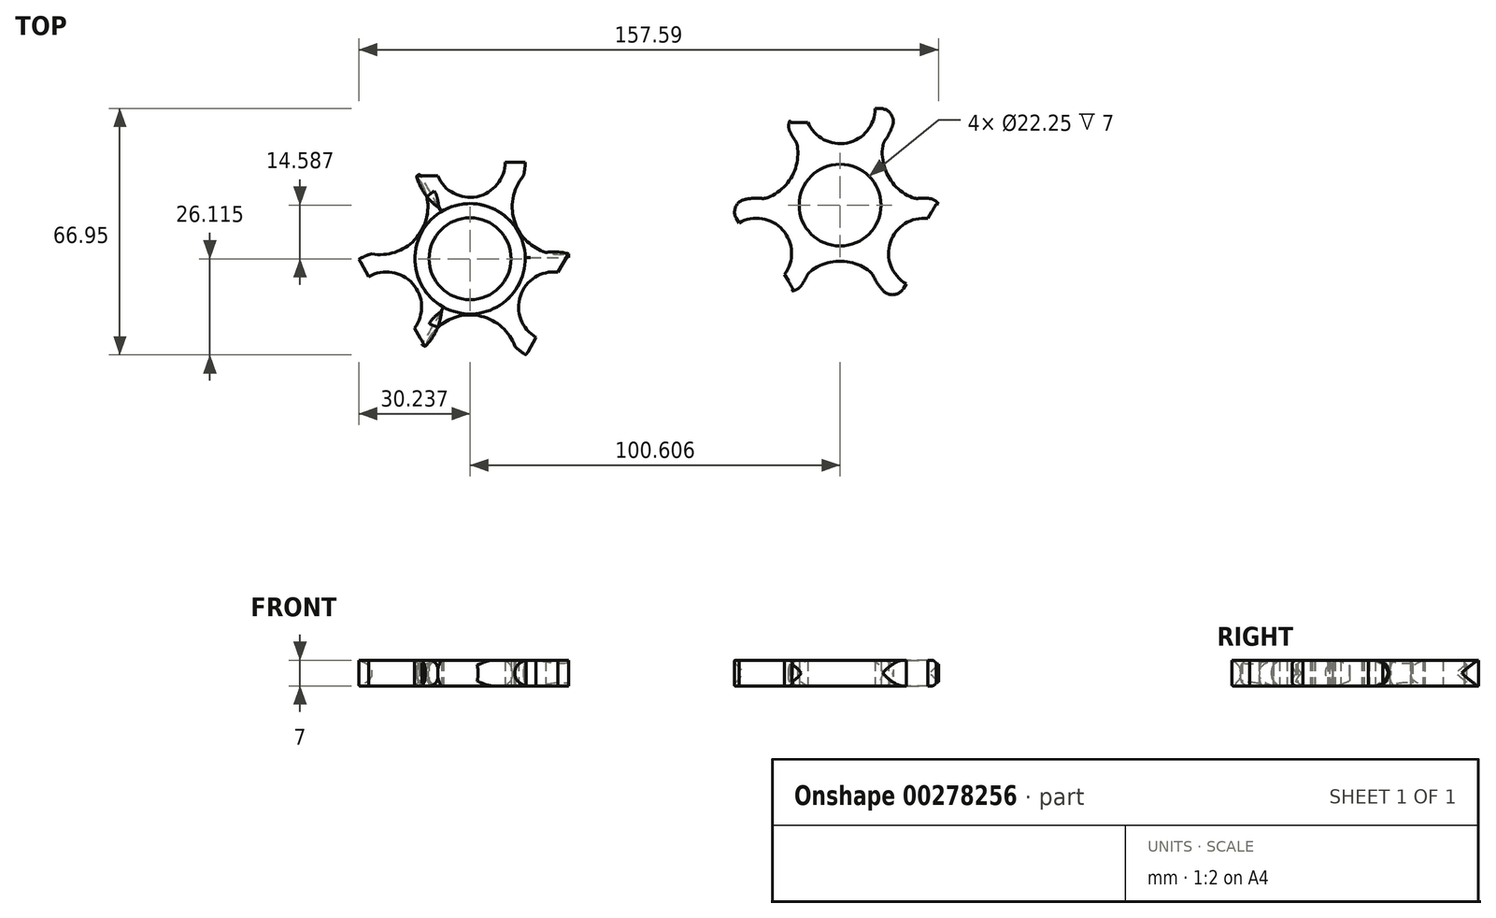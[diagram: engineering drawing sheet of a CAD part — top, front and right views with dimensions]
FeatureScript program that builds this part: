
annotation { "Feature Type Name" : "Feature", "Feature Type Description" : "" }
export const myFeature = defineFeature(function(context is Context, id is Id, definition is map)
    precondition{}
    {
        {
            var Q0;
            Q0=qCreatedBy(makeId("Top.planeOp"),FACE);
            var sketch = newSketch(context, id + "F0", { "sketchPlane" : qUnion([Q0])});
            skCircle(sketch, "E0", {"center": v(37.2, 27.44) * mm, "radius": 15 * mm});
            skLineSegment(sketch, "E1", {"start": v(37.2, 12.44) * mm, "end": v(37.2, 1.2) * mm});
            skCircle(sketch, "E2", {"center": v(37.2, 1.2) * mm, "radius": 15 * mm});
            skCircle(sketch, "E3", {"center": v(37.2, 1.2) * mm, "radius": 11.12 * mm});
            skLineSegment(sketch, "E4", {"start": v(37.2, 27.44) * mm, "end": v(22.2, 27.44) * mm});
            skLineSegment(sketch, "E5", {"start": v(22.2, 27.44) * mm, "end": v(37.2, 27.44) * mm});
            skLineSegment(sketch, "E6", {"start": v(37.2, 27.44) * mm, "end": v(52.2, 27.44) * mm});
            skLineSegment(sketch, "E7", {"start": v(37.2, 27.44) * mm, "end": v(25.65, 17.88) * mm, "construction": true});
            skLineSegment(sketch, "E8", {"start": v(25.65, 17.88) * mm, "end": v(31.43, 22.66) * mm, "construction": true});
            skLineSegment(sketch, "E9", {"start": v(37.2, 16.2) * mm, "end": v(37.2, 23.7) * mm});
            skLineSegment(sketch, "E10", {"start": v(37.2, 23.7) * mm, "end": v(22.68, 23.7) * mm});
            skLineSegment(sketch, "E11", {"start": v(37.2, 23.7) * mm, "end": v(51.73, 23.7) * mm});
            skArc(sketch, "E12", {"start": v(51.73, 23.7) * mm, "mid": v(50.41, 8.82) * mm, "end": v(63.95, 2.52) * mm});
            skPoint(sketch, "E13.0.midPoint", {"position": v(37.2, 21.1) * mm});
            skLineSegment(sketch, "E14", {"start": v(63.95, 2.52) * mm, "end": v(63.95, 1.52) * mm});
            skLineSegment(sketch, "E15", {"start": v(63.95, 1.52) * mm, "end": v(52.2, 1.52) * mm});
            skCircle(sketch, "E16", {"center": v(37.2, 27.44) * mm, "radius": 9.55 * mm});
            skArc(sketch, "E17", {"start": v(14.91, 28.25) * mm, "mid": v(13.6, 13.38) * mm, "end": v(27.14, 7.08) * mm});
            skLineSegment(sketch, "E18", {"start": v(63.95, 2.52) * mm, "end": v(37.2, 2.52) * mm});
            skLineSegment(sketch, "E19", {"start": v(10.46, 2.52) * mm, "end": v(37.2, 2.52) * mm});
            skLineSegment(sketch, "E20", {"start": v(37.2, 23.7) * mm, "end": v(37.2, 1.2) * mm});
            skArc(sketch, "E21", {"start": v(10.46, 2.52) * mm, "mid": v(24, 8.82) * mm, "end": v(22.68, 23.7) * mm});
            skSolve(sketch);
        }
        {
            var Q0;
            {var subQ0=sQuery(id+"F0.wireOp",EDGE,"E5");var subQ1=sQuery(id+"F0.wireOp",EDGE,"E0");var subQ2=makeQuery(id+"F0.imprint","INTERSECT",VERTEX,{"derivedFrom":[subQ1,subQ0]});Q0=makeQuery(id+"F0.imprint","IMPRINT",FACE,{"disambiguationData":[TD([[makeQuery(id+"F0.imprint","IMPRINT",EDGE,{"disambiguationData":[TD([[subQ2,1.0]])],"derivedFrom":subQ1}),1.0]])]});}
            var Q1;
            {var subQ0=sQuery(id+"F0.wireOp",EDGE,"E5");var subQ1=sQuery(id+"F0.wireOp",EDGE,"E0");var subQ2=makeQuery(id+"F0.imprint","INTERSECT",VERTEX,{"derivedFrom":[subQ1,subQ0]});Q1=makeQuery(id+"F0.imprint","IMPRINT",FACE,{"disambiguationData":[TD([[makeQuery(id+"F0.imprint","IMPRINT",EDGE,{"disambiguationData":[TD([[subQ2,-1.0]])],"derivedFrom":subQ1}),1.0]])]});}
            var Q2;
            {var subQ0=sQuery(id+"F0.wireOp",EDGE,"E12");var subQ2=sQuery(id+"F0.wireOp",EDGE,"E0");var subQ11=makeQuery(id+"F0.imprint","INTERSECT",VERTEX,{"derivedFrom":[subQ2,subQ0]});Q2=makeQuery(id+"F0.imprint","IMPRINT",FACE,{"disambiguationData":[TD([[makeQuery(id+"F0.imprint","IMPRINT",EDGE,{"disambiguationData":[TD([[subQ11,1.0]])],"derivedFrom":subQ2}),1.0]])]});}
            var Q3;
            {var subQ4=sQuery(id+"F0.wireOp",EDGE,"E3");Q3=makeQuery(id+"F0.imprint","IMPRINT",FACE,{"disambiguationData":[TD([[makeQuery(id+"F0.imprint","IMPRINT",EDGE,{"derivedFrom":subQ4}),-1.0]])]});}
            var Q4;
            {var subQ0=sQuery(id+"F0.wireOp",EDGE,"E0");var subQ1=makeQuery(id+"F0.imprint","INTERSECT",VERTEX,{"derivedFrom":[subQ0,sQuery(id+"F0.wireOp",EDGE,"E3")]});Q4=makeQuery(id+"F0.imprint","IMPRINT",FACE,{"disambiguationData":[TD([[makeQuery(id+"F0.imprint","IMPRINT",EDGE,{"disambiguationData":[TD([[subQ1,1.0]])],"derivedFrom":subQ0}),1.0]])]});}
            var Q5;
            {var subQ0=sQuery(id+"F0.wireOp",EDGE,"E6");var subQ1=sQuery(id+"F0.wireOp",EDGE,"E0");var subQ2=makeQuery(id+"F0.imprint","INTERSECT",VERTEX,{"derivedFrom":[subQ1,subQ0]});Q5=makeQuery(id+"F0.imprint","IMPRINT",FACE,{"disambiguationData":[TD([[makeQuery(id+"F0.imprint","IMPRINT",EDGE,{"disambiguationData":[TD([[subQ2,1.0]])],"derivedFrom":subQ0}),-1.0]])]});}
            var Q6;
            {var subQ0=sQuery(id+"F0.wireOp",EDGE,"E14");Q6=makeQuery(id+"F0.imprint","IMPRINT",FACE,{"disambiguationData":[TD([[makeQuery(id+"F0.imprint","IMPRINT",EDGE,{"derivedFrom":subQ0}),-1.0]])]});}
            var Q7;
            {var subQ0=sQuery(id+"F0.wireOp",EDGE,"E2");var subQ1=sQuery(id+"F0.wireOp",EDGE,"E0");var subQ2=makeQuery(id+"F0.imprint","INTERSECT",VERTEX,{"disambiguationData":[OD(1.0)],"derivedFrom":[subQ1,subQ0]});Q7=makeQuery(id+"F0.imprint","IMPRINT",FACE,{"disambiguationData":[TD([[makeQuery(id+"F0.imprint","IMPRINT",EDGE,{"disambiguationData":[TD([[subQ2,-1.0]])],"derivedFrom":subQ0}),1.0]])]});}
            var Q8;
            {var subQ0=sQuery(id+"F0.wireOp",EDGE,"E12");var subQ1=sQuery(id+"F0.wireOp",EDGE,"E0");var subQ2=makeQuery(id+"F0.imprint","INTERSECT",VERTEX,{"derivedFrom":[subQ1,subQ0]});Q8=makeQuery(id+"F0.imprint","IMPRINT",FACE,{"disambiguationData":[TD([[makeQuery(id+"F0.imprint","IMPRINT",EDGE,{"disambiguationData":[TD([[subQ2,1.0]])],"derivedFrom":subQ1}),-1.0]])]});}
            var Q9;
            {var subQ5=sQuery(id+"F0.wireOp",EDGE,"E2");var subQ6=makeQuery(id+"F0.imprint","INTERSECT",VERTEX,{"derivedFrom":[subQ5,sQuery(id+"F0.wireOp",EDGE,"E17")]});Q9=makeQuery(id+"F0.imprint","IMPRINT",FACE,{"disambiguationData":[TD([[makeQuery(id+"F0.imprint","IMPRINT",EDGE,{"disambiguationData":[TD([[subQ6,1.0]])],"derivedFrom":subQ5}),1.0]])]});}
            var Q10;
            {var subQ6=sQuery(id+"F0.wireOp",EDGE,"E0");var subQ9=sQuery(id+"F0.wireOp",EDGE,"E21");var subQ11=makeQuery(id+"F0.imprint","INTERSECT",VERTEX,{"derivedFrom":[subQ6,subQ9]});Q10=makeQuery(id+"F0.imprint","IMPRINT",FACE,{"disambiguationData":[TD([[makeQuery(id+"F0.imprint","IMPRINT",EDGE,{"disambiguationData":[TD([[subQ11,-1.0]])],"derivedFrom":subQ6}),1.0]])]});}
            var Q11;
            {var subQ0=sQuery(id+"F0.wireOp",EDGE,"E21");var subQ1=sQuery(id+"F0.wireOp",EDGE,"E0");var subQ2=makeQuery(id+"F0.imprint","INTERSECT",VERTEX,{"derivedFrom":[subQ1,subQ0]});Q11=makeQuery(id+"F0.imprint","IMPRINT",FACE,{"disambiguationData":[TD([[makeQuery(id+"F0.imprint","IMPRINT",EDGE,{"disambiguationData":[TD([[subQ2,-1.0]])],"derivedFrom":subQ1}),-1.0]])]});}
            var Q12;
            {var subQ5=sQuery(id+"F0.wireOp",EDGE,"E2");var subQ7=makeQuery(id+"F0.imprint","INTERSECT",VERTEX,{"derivedFrom":[subQ5,sQuery(id+"F0.wireOp",EDGE,"E15")]});Q12=makeQuery(id+"F0.imprint","IMPRINT",FACE,{"disambiguationData":[TD([[makeQuery(id+"F0.imprint","IMPRINT",EDGE,{"disambiguationData":[TD([[subQ7,-1.0]])],"derivedFrom":subQ5}),1.0]])]});}
            extrude(context, id + "F1", {"entities" : qUnion([Q0, Q1, Q2, Q3, Q4, Q5, Q6, Q7, Q8, Q9, Q10, Q11, Q12]), "depth" : 7 * mm, "offsetDistance" : 25 * mm});
        }
        {
            var Q0;
            Q0=makeQuery(id+"F0.imprint","IMPRINT",FACE,{"disambiguationData":[TD([[makeQuery(id+"F0.imprint","IMPRINT",EDGE,{"derivedFrom":sQuery(id+"F0.wireOp",EDGE,"E3")}),1.0]])]});
            var Q1;
            Q1=sQuery(id+"F0.wireOp",EDGE,"E1");
            extrude(context, id + "F2", {"entities" : qUnion([Q0]), "bodyType" : ExtendedToolBodyType.SURFACE, "surfaceEntities" : qUnion([Q1]), "depth" : 25 * mm, "offsetDistance" : 25 * mm});
        }
        {
            var Q0;
            Q0=makeQuery(id+"F1.opExtrude","SWEPT_BODY",BODY,{"disambiguationData":[OSD([sQuery(id+"F0.wireOp",EDGE,"E0"),sQuery(id+"F0.wireOp",EDGE,"E2"),sQuery(id+"F0.wireOp",EDGE,"E3"),sQuery(id+"F0.wireOp",EDGE,"E12"),sQuery(id+"F0.wireOp",EDGE,"E14"),sQuery(id+"F0.wireOp",EDGE,"E15"),sQuery(id+"F0.wireOp",EDGE,"E16")])]});
            var Q1;
            Q1=makeQuery(id+"F2.opExtrude","SWEPT_EDGE",EDGE,{"disambiguationData":[OSD([sQuery(id+"F0.wireOp",VERTEX,"E1.end")])]});
            circularPattern(context, id + "F3", {"entities" : qUnion([Q0]), "axis" : qUnion([Q1]), "angle" : 360 * degree, "instanceCount" : 3, "equalSpace" : true, "computeTransformsWithoutBuiltin" : true});
        }
        {
            var Q0;
            Q0=makeQuery(id+"F3.opPattern","COPY",BODY,{"derivedFrom":makeQuery(id+"F1.opExtrude","SWEPT_BODY",BODY,{"disambiguationData":[OSD([sQuery(id+"F0.wireOp",EDGE,"E0"),sQuery(id+"F0.wireOp",EDGE,"E2"),sQuery(id+"F0.wireOp",EDGE,"E3"),sQuery(id+"F0.wireOp",EDGE,"E12"),sQuery(id+"F0.wireOp",EDGE,"E14"),sQuery(id+"F0.wireOp",EDGE,"E15"),sQuery(id+"F0.wireOp",EDGE,"E16"),sQuery(id+"F0.wireOp",EDGE,"E17"),sQuery(id+"F0.wireOp",EDGE,"E21")])]}),"instanceName":"2"});
            var Q1;
            Q1=makeQuery(id+"F1.opExtrude","SWEPT_BODY",BODY,{"disambiguationData":[OSD([sQuery(id+"F0.wireOp",EDGE,"E0"),sQuery(id+"F0.wireOp",EDGE,"E2"),sQuery(id+"F0.wireOp",EDGE,"E3"),sQuery(id+"F0.wireOp",EDGE,"E12"),sQuery(id+"F0.wireOp",EDGE,"E14"),sQuery(id+"F0.wireOp",EDGE,"E15"),sQuery(id+"F0.wireOp",EDGE,"E16"),sQuery(id+"F0.wireOp",EDGE,"E17"),sQuery(id+"F0.wireOp",EDGE,"E21")])]});
            var Q2;
            Q2=makeQuery(id+"F3.opPattern","COPY",BODY,{"derivedFrom":makeQuery(id+"F1.opExtrude","SWEPT_BODY",BODY,{"disambiguationData":[OSD([sQuery(id+"F0.wireOp",EDGE,"E0"),sQuery(id+"F0.wireOp",EDGE,"E2"),sQuery(id+"F0.wireOp",EDGE,"E3"),sQuery(id+"F0.wireOp",EDGE,"E12"),sQuery(id+"F0.wireOp",EDGE,"E14"),sQuery(id+"F0.wireOp",EDGE,"E15"),sQuery(id+"F0.wireOp",EDGE,"E16"),sQuery(id+"F0.wireOp",EDGE,"E17"),sQuery(id+"F0.wireOp",EDGE,"E21")])]}),"instanceName":"1"});
            booleanBodies(context, id + "F4", {"operationType" : BooleanOperationType.UNION, "tools" : qUnion([Q0, Q1, Q2])});
        }
        {
            var Q0;
            Q0=makeQuery(id+"F4.opBoolean","MERGE",FACE,{"derivedFrom":[makeQuery(id+"F1.opExtrude","SWEPT_FACE",FACE,{"disambiguationData":[OSD([sQuery(id+"F0.wireOp",EDGE,"E21")])]}),makeQuery(id+"F3.opPattern","COPY",FACE,{"derivedFrom":makeQuery(id+"F1.opExtrude","SWEPT_FACE",FACE,{"disambiguationData":[OSD([sQuery(id+"F0.wireOp",EDGE,"E12")])]}),"instanceName":"1"})]});
            var Q1;
            Q1=makeQuery(id+"F3.opPattern","COPY",FACE,{"derivedFrom":makeQuery(id+"F1.opExtrude","SWEPT_FACE",FACE,{"disambiguationData":[OSD([sQuery(id+"F0.wireOp",EDGE,"E0")])]}),"instanceName":"1"});
            var Q2;
            Q2=makeQuery(id+"F1.opExtrude","SWEPT_FACE",FACE,{"disambiguationData":[OSD([sQuery(id+"F0.wireOp",EDGE,"E0")])]});
            var Q3;
            Q3=makeQuery(id+"F4.opBoolean","MERGE",FACE,{"derivedFrom":[makeQuery(id+"F1.opExtrude","SWEPT_FACE",FACE,{"disambiguationData":[OSD([sQuery(id+"F0.wireOp",EDGE,"E12")])]}),makeQuery(id+"F3.opPattern","COPY",FACE,{"derivedFrom":makeQuery(id+"F1.opExtrude","SWEPT_FACE",FACE,{"disambiguationData":[OSD([sQuery(id+"F0.wireOp",EDGE,"E21")])]}),"instanceName":"2"})]});
            var Q4;
            Q4=makeQuery(id+"F3.opPattern","COPY",FACE,{"derivedFrom":makeQuery(id+"F1.opExtrude","SWEPT_FACE",FACE,{"disambiguationData":[OSD([sQuery(id+"F0.wireOp",EDGE,"E12")])]}),"instanceName":"2"});
            var Q5;
            Q5=makeQuery(id+"F3.opPattern","COPY",FACE,{"derivedFrom":makeQuery(id+"F1.opExtrude","SWEPT_FACE",FACE,{"disambiguationData":[OSD([sQuery(id+"F0.wireOp",EDGE,"E0")])]}),"instanceName":"2"});
            fillet(context, id + "F5", {"entities" : qUnion([Q0, Q1, Q2, Q3, Q4, Q5]), "radius" : 3.5 * mm, "tangentPropagation" : true, "allowEdgeOverflow" : false});
        }
        {
            var Q0;
            Q0=qCreatedBy(makeId("Top.planeOp"),FACE);
            var sketch = newSketch(context, id + "F6", { "sketchPlane" : qUnion([Q0])});
            skCircle(sketch, "E22", {"center": v(-63.4, 12.86) * mm, "radius": 15 * mm});
            skLineSegment(sketch, "E23", {"start": v(-63.4, -2.14) * mm, "end": v(-63.4, -13.4) * mm});
            skCircle(sketch, "E24", {"center": v(-63.4, -13.4) * mm, "radius": 15 * mm});
            skCircle(sketch, "E25", {"center": v(-63.4, -13.4) * mm, "radius": 11.12 * mm});
            skLineSegment(sketch, "E26", {"start": v(-63.4, 12.86) * mm, "end": v(-78.4, 12.86) * mm});
            skLineSegment(sketch, "E27", {"start": v(-78.4, 12.86) * mm, "end": v(-63.4, 12.86) * mm});
            skLineSegment(sketch, "E28", {"start": v(-63.4, 12.86) * mm, "end": v(-48.4, 12.86) * mm});
            skLineSegment(sketch, "E29", {"start": v(-63.4, 12.86) * mm, "end": v(-74.96, 3.29) * mm, "construction": true});
            skLineSegment(sketch, "E30", {"start": v(-74.96, 3.29) * mm, "end": v(-69.18, 8.07) * mm, "construction": true});
            skLineSegment(sketch, "E31", {"start": v(-63.4, 1.6) * mm, "end": v(-63.4, 9.1) * mm});
            skLineSegment(sketch, "E32", {"start": v(-63.4, 9.1) * mm, "end": v(-77.93, 9.1) * mm});
            skLineSegment(sketch, "E33", {"start": v(-63.4, 9.1) * mm, "end": v(-48.88, 9.1) * mm});
            skArc(sketch, "E34", {"start": v(-48.88, 9.1) * mm, "mid": v(-50.2, -5.77) * mm, "end": v(-36.66, -12.07) * mm});
            skPoint(sketch, "E35.0.midPoint", {"position": v(-63.4, 6.5) * mm});
            skLineSegment(sketch, "E36", {"start": v(-36.66, -12.07) * mm, "end": v(-36.66, -13.07) * mm});
            skLineSegment(sketch, "E37", {"start": v(-36.66, -13.07) * mm, "end": v(-48.4, -13.07) * mm});
            skCircle(sketch, "E38", {"center": v(-63.4, 12.86) * mm, "radius": 9.55 * mm});
            skArc(sketch, "E39", {"start": v(-85.7, 13.66) * mm, "mid": v(-87, -1.21) * mm, "end": v(-73.47, -7.51) * mm});
            skLineSegment(sketch, "E40", {"start": v(-36.66, -12.07) * mm, "end": v(-63.4, -12.07) * mm});
            skLineSegment(sketch, "E41", {"start": v(-90.15, -12.07) * mm, "end": v(-63.4, -12.07) * mm});
            skLineSegment(sketch, "E42", {"start": v(-63.4, 9.1) * mm, "end": v(-63.4, -13.4) * mm});
            skArc(sketch, "E43", {"start": v(-90.15, -12.07) * mm, "mid": v(-76.61, -5.77) * mm, "end": v(-77.93, 9.1) * mm});
            skLineSegment(sketch, "E44", {"start": v(-63.4, -13.4) * mm, "end": v(-65.58, -14.12) * mm});
            skSolve(sketch);
        }
        {
            var Q0;
            {var subQ0=sQuery(id+"F6.wireOp",EDGE,"E27");var subQ1=sQuery(id+"F6.wireOp",EDGE,"E22");var subQ2=makeQuery(id+"F6.imprint","INTERSECT",VERTEX,{"derivedFrom":[subQ1,subQ0]});Q0=makeQuery(id+"F6.imprint","IMPRINT",FACE,{"disambiguationData":[TD([[makeQuery(id+"F6.imprint","IMPRINT",EDGE,{"disambiguationData":[TD([[subQ2,1.0]])],"derivedFrom":subQ1}),1.0]])]});}
            var Q1;
            {var subQ0=sQuery(id+"F6.wireOp",EDGE,"E27");var subQ1=sQuery(id+"F6.wireOp",EDGE,"E22");var subQ2=makeQuery(id+"F6.imprint","INTERSECT",VERTEX,{"derivedFrom":[subQ1,subQ0]});Q1=makeQuery(id+"F6.imprint","IMPRINT",FACE,{"disambiguationData":[TD([[makeQuery(id+"F6.imprint","IMPRINT",EDGE,{"disambiguationData":[TD([[subQ2,-1.0]])],"derivedFrom":subQ0}),-1.0]])]});}
            var Q2;
            {var subQ6=sQuery(id+"F6.wireOp",EDGE,"E22");var subQ9=sQuery(id+"F6.wireOp",EDGE,"E43");var subQ11=makeQuery(id+"F6.imprint","INTERSECT",VERTEX,{"derivedFrom":[subQ6,subQ9]});Q2=makeQuery(id+"F6.imprint","IMPRINT",FACE,{"disambiguationData":[TD([[makeQuery(id+"F6.imprint","IMPRINT",EDGE,{"disambiguationData":[TD([[subQ11,-1.0]])],"derivedFrom":subQ6}),1.0]])]});}
            var Q3;
            {var subQ0=sQuery(id+"F6.wireOp",EDGE,"E28");var subQ1=sQuery(id+"F6.wireOp",EDGE,"E22");var subQ2=makeQuery(id+"F6.imprint","INTERSECT",VERTEX,{"derivedFrom":[subQ1,subQ0]});Q3=makeQuery(id+"F6.imprint","IMPRINT",FACE,{"disambiguationData":[TD([[makeQuery(id+"F6.imprint","IMPRINT",EDGE,{"disambiguationData":[TD([[subQ2,1.0]])],"derivedFrom":subQ0}),-1.0]])]});}
            var Q4;
            {var subQ0=sQuery(id+"F6.wireOp",EDGE,"E34");var subQ2=sQuery(id+"F6.wireOp",EDGE,"E22");var subQ4=makeQuery(id+"F6.imprint","INTERSECT",VERTEX,{"derivedFrom":[subQ2,subQ0]});Q4=makeQuery(id+"F6.imprint","IMPRINT",FACE,{"disambiguationData":[TD([[makeQuery(id+"F6.imprint","IMPRINT",EDGE,{"disambiguationData":[TD([[subQ4,1.0]])],"derivedFrom":subQ2}),1.0]])]});}
            var Q5;
            {var subQ0=sQuery(id+"F6.wireOp",EDGE,"E42");var subQ1=sQuery(id+"F6.wireOp",EDGE,"E22");var subQ2=makeQuery(id+"F6.imprint","INTERSECT",VERTEX,{"derivedFrom":[subQ1,subQ0]});Q5=makeQuery(id+"F6.imprint","IMPRINT",FACE,{"disambiguationData":[TD([[makeQuery(id+"F6.imprint","IMPRINT",EDGE,{"disambiguationData":[TD([[subQ2,-1.0]])],"derivedFrom":subQ1}),1.0]])]});}
            var Q6;
            {var subQ0=sQuery(id+"F6.wireOp",EDGE,"E24");var subQ1=sQuery(id+"F6.wireOp",EDGE,"E22");var subQ2=makeQuery(id+"F6.imprint","INTERSECT",VERTEX,{"disambiguationData":[OD(0.0)],"derivedFrom":[subQ1,subQ0]});Q6=makeQuery(id+"F6.imprint","IMPRINT",FACE,{"disambiguationData":[TD([[makeQuery(id+"F6.imprint","IMPRINT",EDGE,{"disambiguationData":[TD([[subQ2,-1.0]])],"derivedFrom":subQ1}),1.0]])]});}
            var Q7;
            {var subQ5=sQuery(id+"F6.wireOp",EDGE,"E24");var subQ7=sQuery(id+"F6.wireOp",EDGE,"E22");var subQ8=makeQuery(id+"F6.imprint","INTERSECT",VERTEX,{"disambiguationData":[OD(0.0)],"derivedFrom":[subQ7,subQ5]});Q7=makeQuery(id+"F6.imprint","IMPRINT",FACE,{"disambiguationData":[TD([[makeQuery(id+"F6.imprint","IMPRINT",EDGE,{"disambiguationData":[TD([[subQ8,-1.0]])],"derivedFrom":subQ7}),-1.0]])]});}
            var Q8;
            {var subQ0=sQuery(id+"F6.wireOp",EDGE,"E42");var subQ5=sQuery(id+"F6.wireOp",EDGE,"E22");var subQ6=makeQuery(id+"F6.imprint","INTERSECT",VERTEX,{"derivedFrom":[subQ5,subQ0]});Q8=makeQuery(id+"F6.imprint","IMPRINT",FACE,{"disambiguationData":[TD([[makeQuery(id+"F6.imprint","IMPRINT",EDGE,{"disambiguationData":[TD([[subQ6,-1.0]])],"derivedFrom":subQ5}),-1.0]])]});}
            var Q9;
            {var subQ0=sQuery(id+"F6.wireOp",EDGE,"E34");var subQ1=sQuery(id+"F6.wireOp",EDGE,"E22");var subQ2=makeQuery(id+"F6.imprint","INTERSECT",VERTEX,{"derivedFrom":[subQ1,subQ0]});Q9=makeQuery(id+"F6.imprint","IMPRINT",FACE,{"disambiguationData":[TD([[makeQuery(id+"F6.imprint","IMPRINT",EDGE,{"disambiguationData":[TD([[subQ2,1.0]])],"derivedFrom":subQ1}),-1.0]])]});}
            var Q10;
            {var subQ0=sQuery(id+"F6.wireOp",EDGE,"E43");var subQ1=sQuery(id+"F6.wireOp",EDGE,"E22");var subQ2=makeQuery(id+"F6.imprint","INTERSECT",VERTEX,{"derivedFrom":[subQ1,subQ0]});Q10=makeQuery(id+"F6.imprint","IMPRINT",FACE,{"disambiguationData":[TD([[makeQuery(id+"F6.imprint","IMPRINT",EDGE,{"disambiguationData":[TD([[subQ2,-1.0]])],"derivedFrom":subQ1}),-1.0]])]});}
            var Q11;
            {var subQ5=sQuery(id+"F6.wireOp",EDGE,"E24");var subQ7=makeQuery(id+"F6.imprint","INTERSECT",VERTEX,{"derivedFrom":[subQ5,sQuery(id+"F6.wireOp",EDGE,"E37")]});Q11=makeQuery(id+"F6.imprint","IMPRINT",FACE,{"disambiguationData":[TD([[makeQuery(id+"F6.imprint","IMPRINT",EDGE,{"disambiguationData":[TD([[subQ7,-1.0]])],"derivedFrom":subQ5}),1.0]])]});}
            var Q12;
            {var subQ4=sQuery(id+"F6.wireOp",EDGE,"E36");Q12=makeQuery(id+"F6.imprint","IMPRINT",FACE,{"disambiguationData":[TD([[makeQuery(id+"F6.imprint","IMPRINT",EDGE,{"derivedFrom":subQ4}),-1.0]])]});}
            extrude(context, id + "F7", {"entities" : qUnion([Q0, Q1, Q2, Q3, Q4, Q5, Q6, Q7, Q8, Q9, Q10, Q11, Q12]), "depth" : 7 * mm, "offsetDistance" : 25 * mm});
        }
        {
            var Q0;
            Q0=sQuery(id+"F6.wireOp",EDGE,"E44");
            extrude(context, id + "F8", {"bodyType" : ExtendedToolBodyType.SURFACE, "surfaceEntities" : qUnion([Q0]), "depth" : 25 * mm, "offsetDistance" : 25 * mm});
        }
        {
            var Q0;
            Q0=makeQuery(id+"F7.opExtrude","SWEPT_BODY",BODY,{"disambiguationData":[OSD([sQuery(id+"F6.wireOp",EDGE,"E22"),sQuery(id+"F6.wireOp",EDGE,"E24"),sQuery(id+"F6.wireOp",EDGE,"E25"),sQuery(id+"F6.wireOp",EDGE,"E34"),sQuery(id+"F6.wireOp",EDGE,"E36"),sQuery(id+"F6.wireOp",EDGE,"E37"),sQuery(id+"F6.wireOp",EDGE,"E38"),sQuery(id+"F6.wireOp",EDGE,"E39"),sQuery(id+"F6.wireOp",EDGE,"E43")])]});
            var Q1;
            Q1=makeQuery(id+"F8.opExtrude","SWEPT_EDGE",EDGE,{"disambiguationData":[OSD([sQuery(id+"F6.wireOp",VERTEX,"E44.start")])]});
            circularPattern(context, id + "F9", {"operationType" : NewBodyOperationType.ADD, "entities" : qUnion([Q0]), "axis" : qUnion([Q1]), "angle" : 360 * degree, "instanceCount" : 3, "equalSpace" : true, "computeTransformsWithoutBuiltin" : true});
        }
        {
            var Q0;
            Q0=makeQuery(id+"F9.boolean.opBoolean","MERGE",EDGE,{"derivedFrom":[makeQuery(id+"F9.opPattern","COPY",EDGE,{"derivedFrom":makeQuery(id+"F7.opExtrude","CAP_EDGE",EDGE,{"disambiguationData":[OSD([sQuery(id+"F6.wireOp",EDGE,"E43")])],"isStart":false}),"instanceName":"1"}),makeQuery(id+"F9.opPattern","COPY",EDGE,{"derivedFrom":makeQuery(id+"F7.opExtrude","CAP_EDGE",EDGE,{"disambiguationData":[OSD([sQuery(id+"F6.wireOp",EDGE,"E34")])],"isStart":false}),"instanceName":"2"})]});
            var Q1;
            Q1=makeQuery(id+"F9.boolean.opBoolean","MERGE",EDGE,{"derivedFrom":[makeQuery(id+"F9.opPattern","COPY",EDGE,{"derivedFrom":makeQuery(id+"F7.opExtrude","CAP_EDGE",EDGE,{"disambiguationData":[OSD([sQuery(id+"F6.wireOp",EDGE,"E43")])],"isStart":true}),"instanceName":"1"}),makeQuery(id+"F9.opPattern","COPY",EDGE,{"derivedFrom":makeQuery(id+"F7.opExtrude","CAP_EDGE",EDGE,{"disambiguationData":[OSD([sQuery(id+"F6.wireOp",EDGE,"E34")])],"isStart":true}),"instanceName":"2"})]});
            var Q2;
            Q2=makeQuery(id+"F7.opExtrude","CAP_EDGE",EDGE,{"disambiguationData":[OSD([sQuery(id+"F6.wireOp",EDGE,"E34")])],"isStart":false});
            var Q3;
            Q3=makeQuery(id+"F7.opExtrude","CAP_EDGE",EDGE,{"disambiguationData":[OSD([sQuery(id+"F6.wireOp",EDGE,"E34")])],"isStart":true});
            var Q4;
            Q4=makeQuery(id+"F9.boolean.opBoolean","MERGE",EDGE,{"derivedFrom":[makeQuery(id+"F7.opExtrude","CAP_EDGE",EDGE,{"disambiguationData":[OSD([sQuery(id+"F6.wireOp",EDGE,"E43")])],"isStart":false}),makeQuery(id+"F9.opPattern","COPY",EDGE,{"derivedFrom":makeQuery(id+"F7.opExtrude","CAP_EDGE",EDGE,{"disambiguationData":[OSD([sQuery(id+"F6.wireOp",EDGE,"E34")])],"isStart":false}),"instanceName":"1"})]});
            var Q5;
            Q5=makeQuery(id+"F9.boolean.opBoolean","MERGE",EDGE,{"derivedFrom":[makeQuery(id+"F7.opExtrude","CAP_EDGE",EDGE,{"disambiguationData":[OSD([sQuery(id+"F6.wireOp",EDGE,"E43")])],"isStart":true}),makeQuery(id+"F9.opPattern","COPY",EDGE,{"derivedFrom":makeQuery(id+"F7.opExtrude","CAP_EDGE",EDGE,{"disambiguationData":[OSD([sQuery(id+"F6.wireOp",EDGE,"E34")])],"isStart":true}),"instanceName":"1"})]});
            fillet(context, id + "F10", {"entities" : qUnion([Q0, Q1, Q2, Q3, Q4, Q5]), "radius" : 3 * mm, "tangentPropagation" : true, "allowEdgeOverflow" : false});
        }
        {
            var Q0;
            Q0=makeQuery(id+"F9.opPattern","COPY",EDGE,{"derivedFrom":makeQuery(id+"F7.opExtrude","CAP_EDGE",EDGE,{"disambiguationData":[OSD([sQuery(id+"F6.wireOp",EDGE,"E22")])],"isStart":false}),"instanceName":"2"});
            var Q1;
            Q1=makeQuery(id+"F9.opPattern","COPY",EDGE,{"derivedFrom":makeQuery(id+"F7.opExtrude","CAP_EDGE",EDGE,{"disambiguationData":[OSD([sQuery(id+"F6.wireOp",EDGE,"E22")])],"isStart":true}),"instanceName":"2"});
            var Q2;
            Q2=makeQuery(id+"F9.opPattern","COPY",EDGE,{"derivedFrom":makeQuery(id+"F7.opExtrude","CAP_EDGE",EDGE,{"disambiguationData":[OSD([sQuery(id+"F6.wireOp",EDGE,"E22")])],"isStart":false}),"instanceName":"1"});
            var Q3;
            Q3=makeQuery(id+"F9.opPattern","COPY",EDGE,{"derivedFrom":makeQuery(id+"F7.opExtrude","CAP_EDGE",EDGE,{"disambiguationData":[OSD([sQuery(id+"F6.wireOp",EDGE,"E22")])],"isStart":true}),"instanceName":"1"});
            var Q4;
            Q4=makeQuery(id+"F7.opExtrude","CAP_EDGE",EDGE,{"disambiguationData":[OSD([sQuery(id+"F6.wireOp",EDGE,"E22")])],"isStart":true});
            var Q5;
            Q5=makeQuery(id+"F7.opExtrude","CAP_EDGE",EDGE,{"disambiguationData":[OSD([sQuery(id+"F6.wireOp",EDGE,"E22")])],"isStart":false});
            fillet(context, id + "F11", {"entities" : qUnion([Q0, Q1, Q2, Q3, Q4, Q5]), "radius" : 2.5 * mm, "tangentPropagation" : true, "allowEdgeOverflow" : false});
        }
    });
